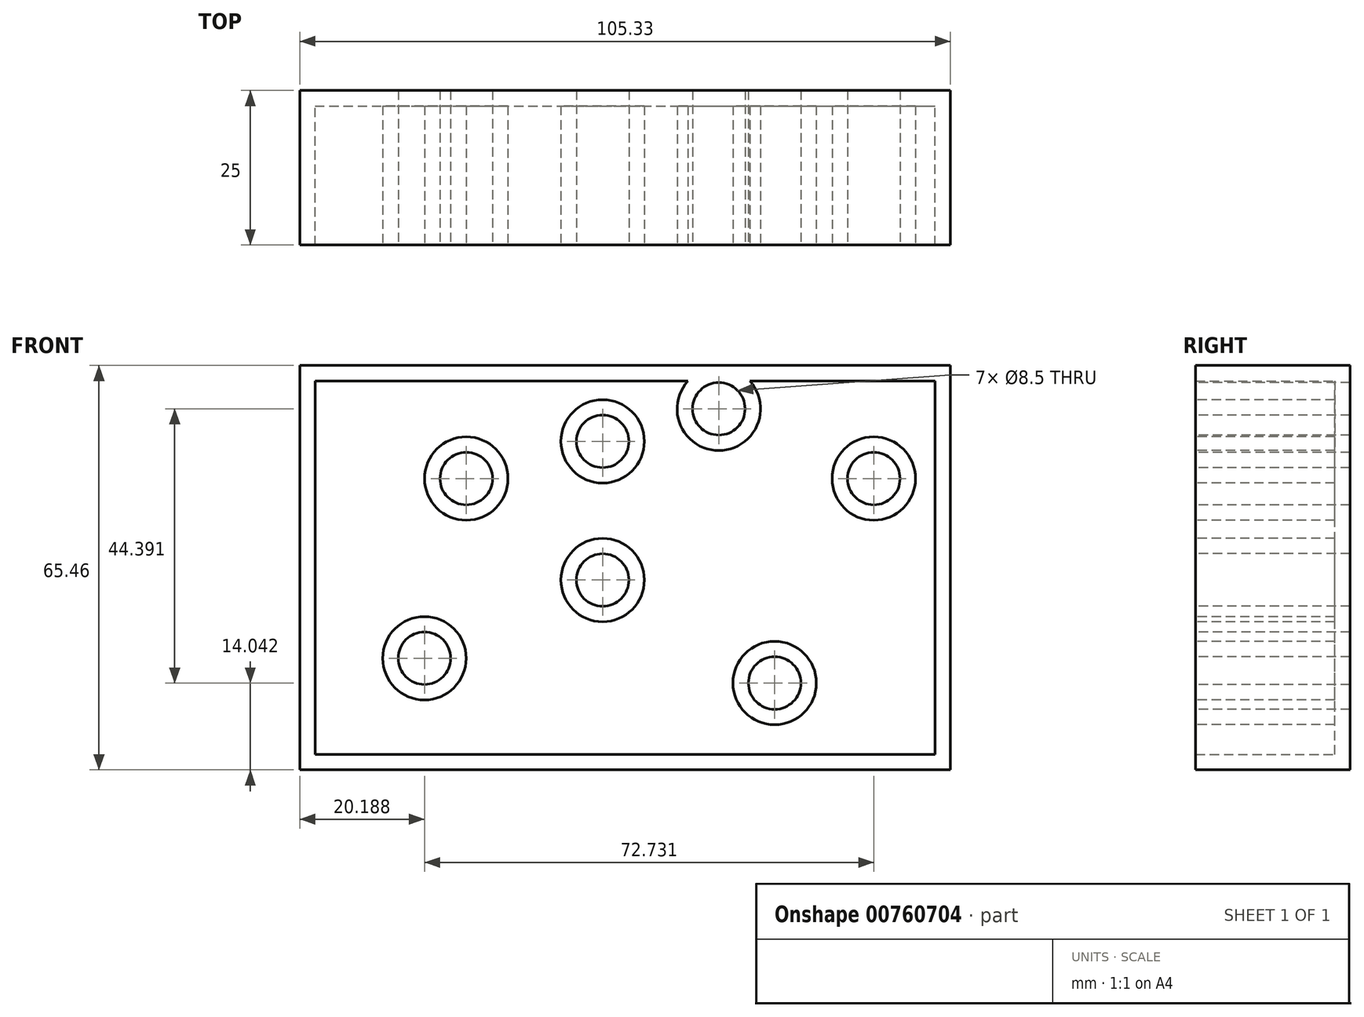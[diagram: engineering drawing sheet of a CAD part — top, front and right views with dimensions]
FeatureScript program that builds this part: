
annotation { "Feature Type Name" : "Feature", "Feature Type Description" : "" }
export const myFeature = defineFeature(function(context is Context, id is Id, definition is map)
    precondition{}
    {
        {
            var Q0;
            Q0=qCreatedBy(makeId("Front.planeOp"),FACE);
            var sketch = newSketch(context, id + "F0", { "sketchPlane" : qUnion([Q0])});
            skLineSegment(sketch, "E0.bottom", {"start": v(-49.03, -30.72) * mm, "end": v(56.3, -30.72) * mm});
            skLineSegment(sketch, "E0.top", {"start": v(-49.03, 34.74) * mm, "end": v(56.3, 34.74) * mm});
            skLineSegment(sketch, "E0.left", {"start": v(-49.03, -30.72) * mm, "end": v(-49.03, 34.74) * mm});
            skLineSegment(sketch, "E0.right", {"start": v(56.3, -30.72) * mm, "end": v(56.3, 34.74) * mm});
            skPoint(sketch, "E1", {"position": v(-22.45, 0) * mm});
            skPoint(sketch, "E2", {"position": v(0, 0) * mm});
            skPoint(sketch, "E3", {"position": v(25.46, 0) * mm});
            skPoint(sketch, "E4", {"position": v(25.46, 20.44) * mm});
            skPoint(sketch, "E5", {"position": v(0, 23.7) * mm});
            skPoint(sketch, "E6", {"position": v(-22.45, 23.2) * mm});
            skPoint(sketch, "E7", {"position": v(-32.85, -19.69) * mm});
            skPoint(sketch, "E8", {"position": v(12.8, -17.68) * mm});
            skPoint(sketch, "E9", {"position": v(39.38, -20.44) * mm});
            skPoint(sketch, "E10", {"position": v(45.9, 10.16) * mm});
            skPoint(sketch, "E11", {"position": v(43.39, 28.47) * mm});
            skPoint(sketch, "E12", {"position": v(-39.38, 28.47) * mm});
            skPoint(sketch, "E13", {"position": v(-39.38, -14.67) * mm});
            skSolve(sketch);
        }
        {
            var Q0;
            Q0 = qSketchRegion(id + "F0", true);
            extrude(context, id + "F1", {"entities" : qUnion([Q0]), "depth" : 25 * mm, "offsetDistance" : 25 * mm});
        }
        {
            var Q0;
            Q0=makeQuery(id+"F1.opExtrude","CAP_FACE",FACE,{"disambiguationData":[OSD([sQuery(id+"F0.wireOp",EDGE,"E0.bottom"),sQuery(id+"F0.wireOp",EDGE,"E0.top"),sQuery(id+"F0.wireOp",EDGE,"E0.left"),sQuery(id+"F0.wireOp",EDGE,"E0.right")])],"isStart":false});
            var sketch = newSketch(context, id + "F2", { "sketchPlane" : qUnion([Q0])});
            skPoint(sketch, "E14", {"position": v(0, 0) * mm});
            skPoint(sketch, "E15", {"position": v(-22.07, 16.43) * mm});
            skPoint(sketch, "E16", {"position": v(-28.84, -12.67) * mm});
            skPoint(sketch, "E17", {"position": v(27.84, -16.68) * mm});
            skPoint(sketch, "E18", {"position": v(43.89, 16.43) * mm});
            skPoint(sketch, "E19", {"position": v(18.8, 27.71) * mm});
            skPoint(sketch, "E20", {"position": v(0, 22.45) * mm});
            skSolve(sketch);
        }
        {
            var Q0;
            Q0=sQuery(id+"F2.wireOp",VERTEX,"E15");
            var Q1;
            Q1=sQuery(id+"F2.wireOp",VERTEX,"E20");
            var Q2;
            Q2=sQuery(id+"F2.wireOp",VERTEX,"E19");
            var Q3;
            Q3=sQuery(id+"F2.wireOp",VERTEX,"E18");
            var Q4;
            Q4=sQuery(id+"F2.wireOp",VERTEX,"E16");
            var Q5;
            Q5=sQuery(id+"F2.wireOp",VERTEX,"E14");
            var Q6;
            Q6=sQuery(id+"F2.wireOp",VERTEX,"E17");
            var Q7;
            Q7=makeQuery(id+"F1.opExtrude","SWEPT_BODY",BODY,{"disambiguationData":[OSD([sQuery(id+"F0.wireOp",EDGE,"E0.bottom"),sQuery(id+"F0.wireOp",EDGE,"E0.top"),sQuery(id+"F0.wireOp",EDGE,"E0.left"),sQuery(id+"F0.wireOp",EDGE,"E0.right")])]});
            hole(context, id + "F3", {"style" : HoleStyle.SIMPLE, "endStyle" : HoleEndStyle.THROUGH, "standardTappedOrClearance" : lookupTablePath({ "standard" : "ISO", "engagement" : "75%", "pitch" : "1.5 mm", "size" : "M10", "type" : "Tapped" }), "standardBlindInLast" : lookupTablePath({ "standard" : "ISO", "engagement" : "75%", "pitch" : "1.5 mm", "size" : "M10", "type" : "Tapped" }), "holeDiameter" : 8.5 * mm, "majorDiameter" : 10 * mm, "showTappedDepth" : true, "isTappedThrough" : true, "tappedDepth" : 27.6 * mm, "tapClearance" : 3, "startFromSketch" : true, "locations" : qUnion([Q0, Q1, Q2, Q3, Q4, Q5, Q6]), "scope" : qUnion([Q7])});
        }
        {
            var Q0;
            Q0=makeQuery(id+"F1.opExtrude","CAP_FACE",FACE,{"disambiguationData":[OSD([sQuery(id+"F0.wireOp",EDGE,"E0.bottom"),sQuery(id+"F0.wireOp",EDGE,"E0.top"),sQuery(id+"F0.wireOp",EDGE,"E0.left"),sQuery(id+"F0.wireOp",EDGE,"E0.right")])],"isStart":false});
            shell(context, id + "F4", {"entities" : qUnion([Q0]), "thickness" : 2.5 * mm});
        }
    });
